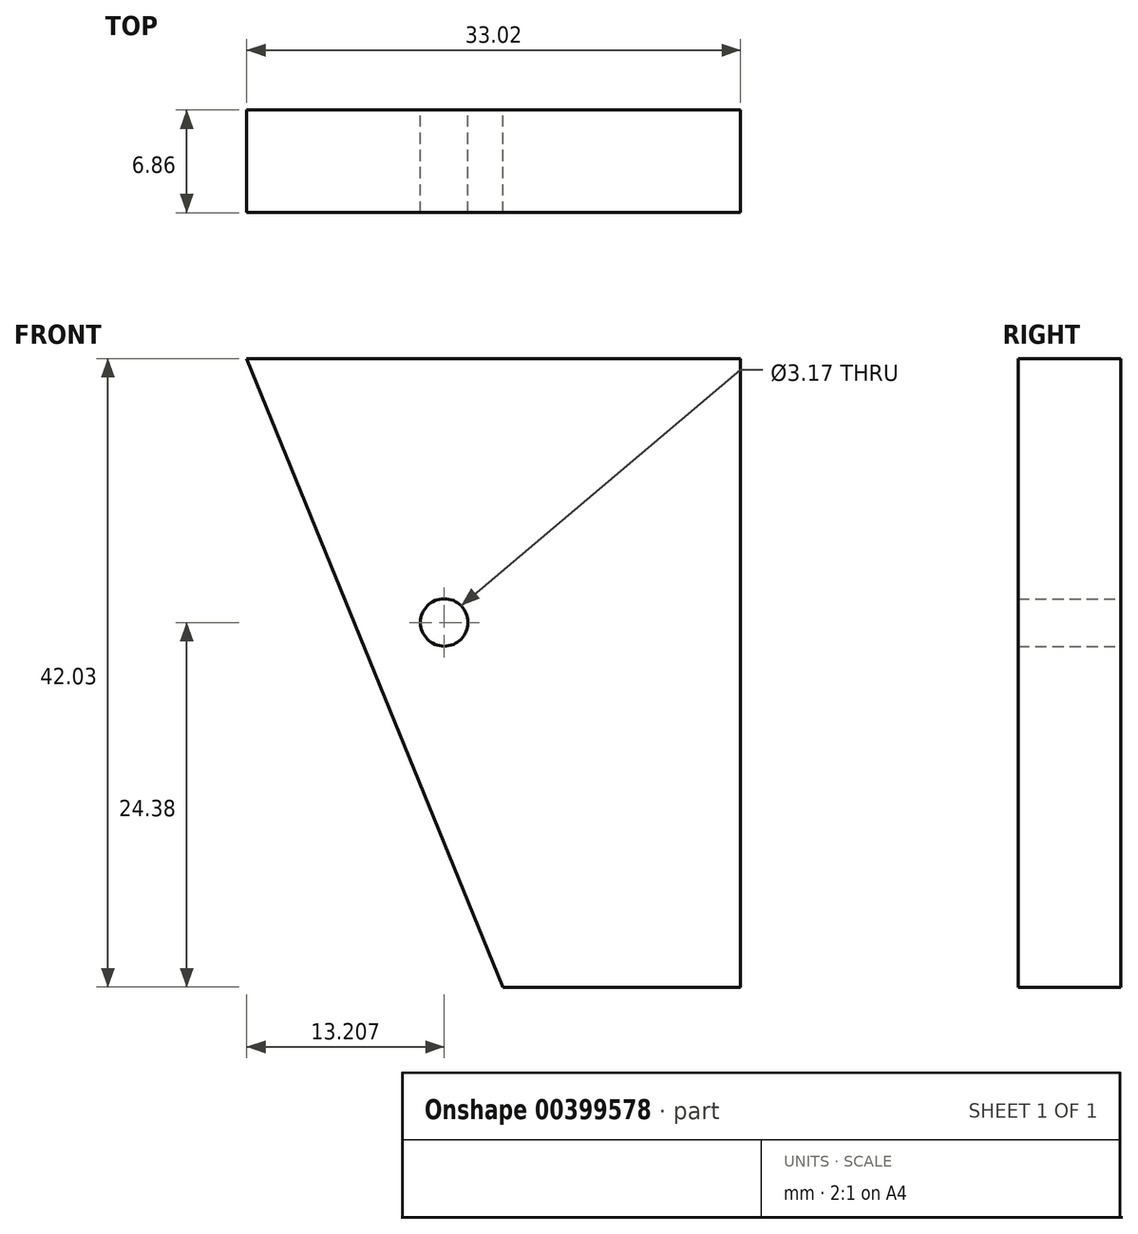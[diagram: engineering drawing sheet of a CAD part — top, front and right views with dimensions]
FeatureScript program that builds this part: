
annotation { "Feature Type Name" : "Feature", "Feature Type Description" : "" }
export const myFeature = defineFeature(function(context is Context, id is Id, definition is map)
    precondition{}
    {
        {
            var Q0;
            Q0=qCreatedBy(makeId("Front.planeOp"),FACE);
            var sketch = newSketch(context, id + "F0", { "sketchPlane" : qUnion([Q0])});
            skLineSegment(sketch, "E0", {"start": v(20.6, 17.23) * mm, "end": v(20.6, -24.8) * mm});
            skLineSegment(sketch, "E1", {"start": v(20.6, 17.23) * mm, "end": v(-12.41, 17.23) * mm});
            skLineSegment(sketch, "E2", {"start": v(20.6, -24.8) * mm, "end": v(4.73, -24.8) * mm});
            skLineSegment(sketch, "E3", {"start": v(4.73, -24.8) * mm, "end": v(-12.41, 17.23) * mm});
            skLineSegment(sketch, "E4", {"start": v(20.6, -24.8) * mm, "end": v(0.8, -24.8) * mm});
            skLineSegment(sketch, "E5", {"start": v(0.8, -24.8) * mm, "end": v(0.8, -0.42) * mm});
            skCircle(sketch, "E6", {"center": v(0.8, -0.42) * mm, "radius": 1.59 * mm});
            skSolve(sketch);
        }
        {
            var Q0;
            {var subQ5=sQuery(id+"F0.wireOp",EDGE,"E0");Q0=makeQuery(id+"F0.imprint","IMPRINT",FACE,{"disambiguationData":[TD([[makeQuery(id+"F0.imprint","IMPRINT",EDGE,{"derivedFrom":subQ5}),-1.0]])]});}
            extrude(context, id + "F1", {"entities" : qUnion([Q0]), "endBound" : BoundingType.SYMMETRIC, "depth" : 6.86 * mm});
        }
    });
